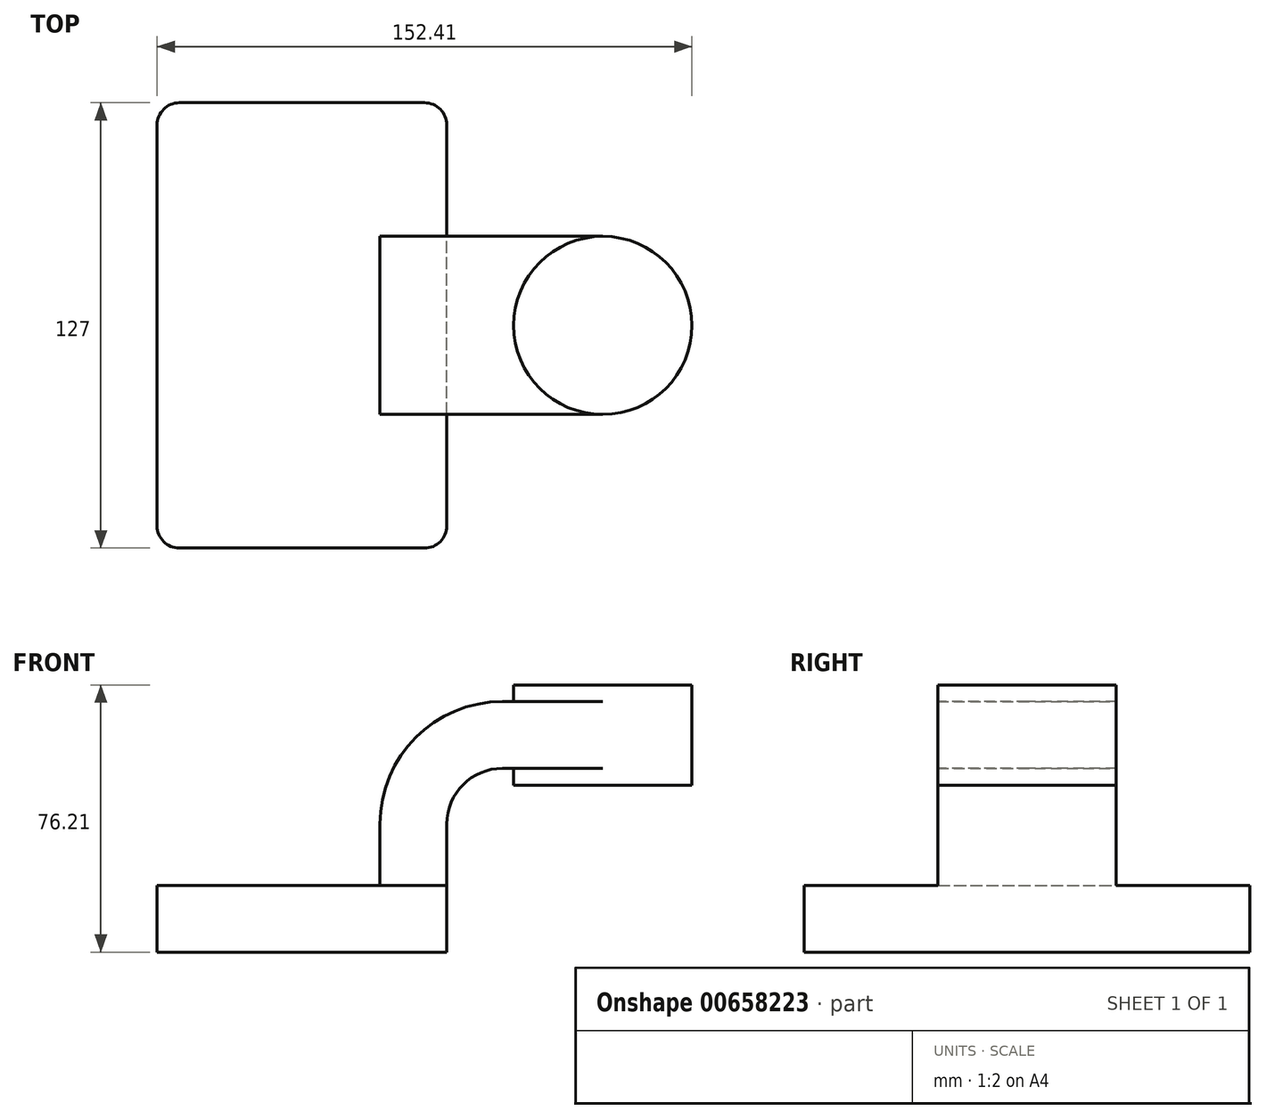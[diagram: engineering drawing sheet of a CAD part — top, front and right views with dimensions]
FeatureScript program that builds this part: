
annotation { "Feature Type Name" : "Feature", "Feature Type Description" : "" }
export const myFeature = defineFeature(function(context is Context, id is Id, definition is map)
    precondition{}
    {
        {
            var Q0;
            Q0=qCreatedBy(makeId("Front.planeOp"),FACE);
            var sketch = newSketch(context, id + "F0", { "sketchPlane" : qUnion([Q0])});
            skLineSegment(sketch, "E0.bottom", {"start": v(-41.28, 9.52) * mm, "end": v(41.28, 9.53) * mm});
            skLineSegment(sketch, "E0.top", {"start": v(-41.28, -9.53) * mm, "end": v(41.28, -9.53) * mm});
            skLineSegment(sketch, "E0.left", {"start": v(-41.28, 9.52) * mm, "end": v(-41.28, -9.53) * mm});
            skLineSegment(sketch, "E0.right", {"start": v(41.28, 9.53) * mm, "end": v(41.28, -9.52) * mm});
            skPoint(sketch, "E0.middle", {"position": v(0, 0) * mm});
            skLineSegment(sketch, "E1.bottom", {"start": v(111.12, 38.1) * mm, "end": v(60.32, 38.1) * mm});
            skLineSegment(sketch, "E1.top", {"start": v(111.12, 66.68) * mm, "end": v(60.32, 66.68) * mm});
            skLineSegment(sketch, "E1.left", {"start": v(111.12, 38.1) * mm, "end": v(111.12, 66.68) * mm});
            skLineSegment(sketch, "E1.right", {"start": v(60.32, 38.1) * mm, "end": v(60.32, 66.68) * mm});
            skPoint(sketch, "E1.middle", {"position": v(85.72, 52.39) * mm});
            skLineSegment(sketch, "E2", {"start": v(41.27, 9.53) * mm, "end": v(41.27, 27) * mm});
            skArc(sketch, "E3", {"start": v(41.27, 27) * mm, "mid": v(45.92, 38.23) * mm, "end": v(57.15, 42.88) * mm});
            skLineSegment(sketch, "E4", {"start": v(57.15, 42.88) * mm, "end": v(85.72, 42.88) * mm});
            skLineSegment(sketch, "E5.0", {"start": v(57.15, 61.93) * mm, "end": v(85.72, 61.93) * mm});
            skArc(sketch, "E5.1", {"start": v(22.22, 27) * mm, "mid": v(32.45, 51.7) * mm, "end": v(57.15, 61.93) * mm});
            skLineSegment(sketch, "E5.2", {"start": v(22.22, 9.53) * mm, "end": v(22.22, 27) * mm});
            skLineSegment(sketch, "E6", {"start": v(85.72, 38.1) * mm, "end": v(85.72, 66.68) * mm});
            skFitSpline(sketch, "E7", {"points": [v(-41.28, 9.52) * mm, v(57.15, 61.93) * mm], "startDerivative": vector(20.52, 115.97) * mm, "endDerivative": vector(143.54, -11.1) * mm});
            skSolve(sketch);
        }
        {
            var Q0;
            Q0=makeQuery(id+"F0.imprint","IMPRINT",FACE,{"disambiguationData":[TD([[makeQuery(id+"F0.imprint","IMPRINT",EDGE,{"derivedFrom":sQuery(id+"F0.wireOp",EDGE,"E0.top")}),1.0]])]});
            extrude(context, id + "F1", {"entities" : qUnion([Q0]), "endBound" : BoundingType.SYMMETRIC, "depth" : 127 * mm, "offsetDistance" : 25.4 * mm});
        }
        {
            var Q0;
            {var subQ1=sQuery(id+"F0.wireOp",EDGE,"E2");Q0=makeQuery(id+"F0.imprint","IMPRINT",FACE,{"disambiguationData":[TD([[makeQuery(id+"F0.imprint","IMPRINT",EDGE,{"derivedFrom":subQ1}),1.0]])]});}
            var Q1;
            {var subQ0=sQuery(id+"F0.wireOp",EDGE,"E4");var subQ1=sQuery(id+"F0.wireOp",EDGE,"E1.right");var subQ2=makeQuery(id+"F0.imprint","INTERSECT",VERTEX,{"derivedFrom":[subQ1,subQ0]});Q1=makeQuery(id+"F0.imprint","IMPRINT",FACE,{"disambiguationData":[TD([[makeQuery(id+"F0.imprint","IMPRINT",EDGE,{"disambiguationData":[TD([[subQ2,-1.0]])],"derivedFrom":subQ1}),-1.0]])]});}
            extrude(context, id + "F2", {"entities" : qUnion([Q0, Q1]), "operationType" : NewBodyOperationType.ADD, "endBound" : BoundingType.SYMMETRIC, "depth" : 50.8 * mm, "offsetDistance" : 25.4 * mm});
        }
        {
            var Q0;
            Q0=makeQuery(id+"F0.imprint","IMPRINT",FACE,{"disambiguationData":[TD([[makeQuery(id+"F0.imprint","IMPRINT",EDGE,{"derivedFrom":sQuery(id+"F0.wireOp",EDGE,"E5.1")}),1.0]])]});
            extrude(context, id + "F3", {"entities" : qUnion([Q0]), "operationType" : NewBodyOperationType.ADD, "endBound" : BoundingType.SYMMETRIC, "depth" : 15.88 * mm, "offsetDistance" : 25.4 * mm});
        }
        {
            var Q0;
            {var subQ4=sQuery(id+"F0.wireOp",EDGE,"E1.left");Q0=makeQuery(id+"F0.imprint","IMPRINT",FACE,{"disambiguationData":[TD([[makeQuery(id+"F0.imprint","IMPRINT",EDGE,{"derivedFrom":subQ4}),1.0]])]});}
            var Q1;
            Q1=sQuery(id+"F0.wireOp",EDGE,"E6");
            revolve(context, id + "F4", {"operationType" : NewBodyOperationType.ADD, "entities" : qUnion([Q0]), "axis" : qUnion([Q1]), "revolveType" : RevolveType.FULL});
        }
        {
            var Q0;
            Q0=makeQuery(id+"F1.opExtrude","CAP_EDGE",EDGE,{"disambiguationData":[OSD([sQuery(id+"F0.wireOp",EDGE,"E0.left")])],"isStart":false});
            var Q1;
            Q1=makeQuery(id+"F1.opExtrude","CAP_EDGE",EDGE,{"disambiguationData":[OSD([sQuery(id+"F0.wireOp",EDGE,"E0.right")])],"isStart":false});
            var Q2;
            Q2=makeQuery(id+"F1.opExtrude","CAP_EDGE",EDGE,{"disambiguationData":[OSD([sQuery(id+"F0.wireOp",EDGE,"E0.right")])],"isStart":true});
            var Q3;
            Q3=makeQuery(id+"F1.opExtrude","CAP_EDGE",EDGE,{"disambiguationData":[OSD([sQuery(id+"F0.wireOp",EDGE,"E0.left")])],"isStart":true});
            fillet(context, id + "F5", {"entities" : qUnion([Q0, Q1, Q2, Q3]), "radius" : 6.35 * mm, "tangentPropagation" : true, "allowEdgeOverflow" : false});
        }
        {
            var Q0;
            Q0=makeQuery(id+"F1.opExtrude","SWEPT_BODY",BODY,{"disambiguationData":[OSD([sQuery(id+"F0.wireOp",EDGE,"E0.bottom"),sQuery(id+"F0.wireOp",EDGE,"E0.top"),sQuery(id+"F0.wireOp",EDGE,"E0.left"),sQuery(id+"F0.wireOp",EDGE,"E0.right")])]});
            transform(context, id + "F6", {"entities" : qUnion([Q0]), "transformType" : TransformType.TRANSLATION_3D, "dx" : 127 * mm, "dy" : 127 * mm, "dz" : 127 * mm, "makeCopy" : true});
        }
        {
            var Q0;
            Q0=makeQuery(id+"F1.opExtrude","SWEPT_BODY",BODY,{"disambiguationData":[OSD([sQuery(id+"F0.wireOp",EDGE,"E0.bottom"),sQuery(id+"F0.wireOp",EDGE,"E0.top"),sQuery(id+"F0.wireOp",EDGE,"E0.left"),sQuery(id+"F0.wireOp",EDGE,"E0.right")])]});
            deleteBodies(context, id + "F7", {"entities" : qUnion([Q0])});
        }
    });
